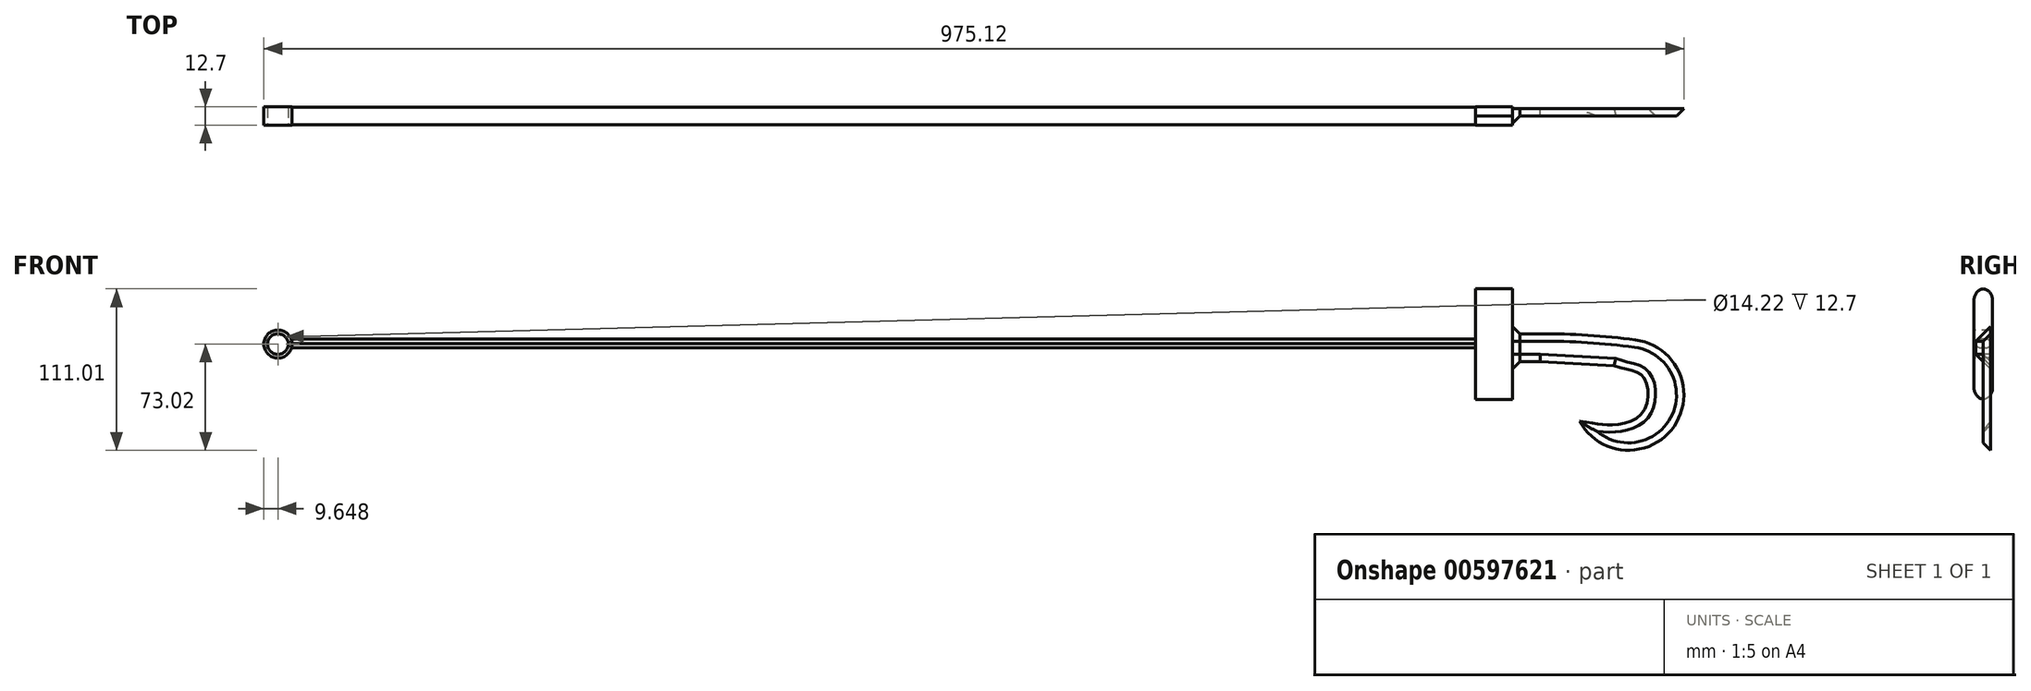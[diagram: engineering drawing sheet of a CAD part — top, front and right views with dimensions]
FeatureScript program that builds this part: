
annotation { "Feature Type Name" : "Feature", "Feature Type Description" : "" }
export const myFeature = defineFeature(function(context is Context, id is Id, definition is map)
    precondition{}
    {
        {
            var Q0;
            Q0=qCreatedBy(makeId("Front.planeOp"),FACE);
            var sketch = newSketch(context, id + "F0", { "sketchPlane" : qUnion([Q0])});
            skCircle(sketch, "E0", {"center": v(-835.15, 0) * mm, "radius": 9.65 * mm});
            skLineSegment(sketch, "E1.bottom", {"start": v(-825.5, 0) * mm, "end": v(-12.7, 0) * mm});
            skLineSegment(sketch, "E1.top", {"start": v(-825.5, 3.5) * mm, "end": v(-12.7, 3.5) * mm});
            skLineSegment(sketch, "E1.left", {"start": v(-825.5, 0) * mm, "end": v(-825.5, 3.5) * mm});
            skLineSegment(sketch, "E1.right", {"start": v(-12.7, 0) * mm, "end": v(-12.7, 3.5) * mm});
            skLineSegment(sketch, "E2.top", {"start": v(-825.5, -2.66) * mm, "end": v(-12.7, -2.66) * mm});
            skLineSegment(sketch, "E2.left", {"start": v(-825.5, 0) * mm, "end": v(-825.5, -2.66) * mm});
            skLineSegment(sketch, "E2.right", {"start": v(-12.7, 0) * mm, "end": v(-12.7, -2.66) * mm});
            skLineSegment(sketch, "E3.bottom", {"start": v(-12.7, 38.1) * mm, "end": v(12.7, 38.1) * mm});
            skLineSegment(sketch, "E3.top", {"start": v(-12.7, -38.1) * mm, "end": v(12.7, -38.1) * mm});
            skLineSegment(sketch, "E3.left", {"start": v(-12.7, 38.1) * mm, "end": v(-12.7, -38.1) * mm});
            skLineSegment(sketch, "E3.right", {"start": v(12.7, 38.1) * mm, "end": v(12.7, -38.1) * mm});
            skPoint(sketch, "E3.middle", {"position": v(0, 0) * mm});
            skLineSegment(sketch, "E4.left", {"start": v(12.7, -7.8) * mm, "end": v(12.7, -17.6) * mm});
            skPoint(sketch, "E4.middle", {"position": v(21.18, 0) * mm});
            skSolve(sketch);
        }
        {
            var Q0;
            Q0 = qSketchRegion(id + "F0", true);
            extrude(context, id + "F1", {"entities" : qUnion([Q0]), "endBound" : BoundingType.SYMMETRIC, "oppositeDirection" : true, "depth" : 12.7 * mm, "offsetDistance" : 25.4 * mm});
        }
        {
            var Q0;
            Q0=makeQuery(id+"F1.opExtrude","CAP_EDGE",EDGE,{"disambiguationData":[OSD([sQuery(id+"F0.wireOp",EDGE,"E1.top")])],"isStart":true});
            var Q1;
            Q1=makeQuery(id+"F1.opExtrude","CAP_EDGE",EDGE,{"disambiguationData":[OSD([sQuery(id+"F0.wireOp",EDGE,"E2.top")])],"isStart":false});
            fillet(context, id + "F2", {"entities" : qUnion([Q0, Q1]), "radius" : 5.08 * mm, "tangentPropagation" : true, "defaultsChanged" : false, "vertexSettings" : [], "allowEdgeOverflow" : false});
        }
        {
            var Q0;
            Q0=makeQuery(id+"F1.opExtrude","CAP_EDGE",EDGE,{"disambiguationData":[OSD([sQuery(id+"F0.wireOp",EDGE,"E1.top")])],"isStart":false});
            fillet(context, id + "F3", {"entities" : qUnion([Q0]), "radius" : 5.08 * mm, "tangentPropagation" : true, "allowEdgeOverflow" : false});
        }
        {
            var Q0;
            Q0=makeQuery(id+"F1.opExtrude","CAP_EDGE",EDGE,{"disambiguationData":[OSD([sQuery(id+"F0.wireOp",EDGE,"E2.top")])],"isStart":true});
            fillet(context, id + "F4", {"entities" : qUnion([Q0]), "radius" : 5.08 * mm, "tangentPropagation" : true, "allowEdgeOverflow" : false});
        }
        {
            var Q0;
            Q0=qCreatedBy(makeId("Front.planeOp"),FACE);
            var sketch = newSketch(context, id + "F5", { "sketchPlane" : qUnion([Q0])});
            skLineSegment(sketch, "E5.bottom", {"start": v(31.7, 7.1) * mm, "end": v(6.3, 7.1) * mm});
            skLineSegment(sketch, "E5.top", {"start": v(31.7, -11.96) * mm, "end": v(6.3, -11.96) * mm});
            skLineSegment(sketch, "E5.left", {"start": v(31.7, 7.1) * mm, "end": v(31.7, -11.96) * mm});
            skLineSegment(sketch, "E5.right", {"start": v(6.3, 7.1) * mm, "end": v(6.3, -11.96) * mm});
            skArc(sketch, "E6", {"start": v(31.7, 7.1) * mm, "mid": v(64.48, 6.03) * mm, "end": v(97.12, 2.86) * mm});
            skArc(sketch, "E7", {"start": v(97.12, 2.86) * mm, "mid": v(123.63, -56.48) * mm, "end": v(58.73, -53.09) * mm});
            skLineSegment(sketch, "E8", {"start": v(31.7, -11.96) * mm, "end": v(82.42, -14.9) * mm});
            skFitSpline(sketch, "E9", {"points": [v(82.42, -14.9) * mm, v(102.25, -22.24) * mm, v(102.25, -46.86) * mm, v(79.31, -55.53) * mm, v(58.73, -53.09) * mm], "startDerivative": vector(101.25, -41.64) * mm, "endDerivative": vector(-126.14, 14.62) * mm});
            skSolve(sketch);
        }
        {
            var Q0;
            Q0 = qSketchRegion(id + "F5", true);
            extrude(context, id + "F6", {"entities" : qUnion([Q0]), "operationType" : NewBodyOperationType.ADD, "oppositeDirection" : true, "depth" : 5.08 * mm, "offsetDistance" : 25.4 * mm});
        }
        {
            var Q0;
            Q0=makeQuery(id+"F6.opExtrude","CAP_FACE",FACE,{"disambiguationData":[OSD([sQuery(id+"F5.wireOp",EDGE,"E5.bottom"),sQuery(id+"F5.wireOp",EDGE,"E5.top"),sQuery(id+"F5.wireOp",EDGE,"E5.right"),sQuery(id+"F5.wireOp",EDGE,"E6"),sQuery(id+"F5.wireOp",EDGE,"E7"),sQuery(id+"F5.wireOp",EDGE,"E8"),sQuery(id+"F5.wireOp",EDGE,"E9")])],"isStart":true});
            chamfer(context, id + "F7", {"entities" : qUnion([Q0]), "width" : 5.08 * mm, "tangentPropagation" : true});
        }
        {
            var Q0;
            Q0=makeQuery(id+"F1.opExtrude","CAP_FACE",FACE,{"disambiguationData":[OSD([sQuery(id+"F0.wireOp",EDGE,"E0")])],"isStart":true});
            var Q1;
            Q1=makeQuery(id+"F1.opExtrude","CAP_FACE",FACE,{"disambiguationData":[OSD([sQuery(id+"F0.wireOp",EDGE,"E0")])],"isStart":false});
            var Q2;
            Q2=makeQuery(id+"F1.opExtrude","SWEPT_BODY",BODY,{"disambiguationData":[OSD([sQuery(id+"F0.wireOp",EDGE,"E0")])]});
            shell(context, id + "F8", {"entities" : qUnion([Q0, Q1]), "parts" : qUnion([Q2]), "thickness" : 2.54 * mm});
        }
        {
            var Q0;
            Q0=makeQuery(id+"F1.opExtrude","CAP_EDGE",EDGE,{"disambiguationData":[OSD([sQuery(id+"F0.wireOp",EDGE,"E3.bottom")])],"isStart":false});
            var Q1;
            Q1=makeQuery(id+"F1.opExtrude","CAP_EDGE",EDGE,{"disambiguationData":[OSD([sQuery(id+"F0.wireOp",EDGE,"E3.bottom")])],"isStart":true});
            var Q2;
            Q2=makeQuery(id+"F1.opExtrude","CAP_EDGE",EDGE,{"disambiguationData":[OSD([sQuery(id+"F0.wireOp",EDGE,"E3.top")])],"isStart":false});
            var Q3;
            Q3=makeQuery(id+"F1.opExtrude","CAP_EDGE",EDGE,{"disambiguationData":[OSD([sQuery(id+"F0.wireOp",EDGE,"E3.top")])],"isStart":true});
            fillet(context, id + "F9", {"entities" : qUnion([Q0, Q1, Q2, Q3]), "radius" : 7.62 * mm, "tangentPropagation" : true, "allowEdgeOverflow" : false});
        }
    });
